# Revit family: TemID_Кронштейн настенный для биометрических терминалов_Rots-03 Stand
name_source: partatom
category: Охранная сигнализация
units: mm (PartAtom-declared; Revit-internal decimal feet)

## family parameters
Всегда вертикально = Нет
На основе рабочей плоскости = Нет
Общий = Да
При загрузке вырезать с полостями = Нет
Размер круглого соединителя = Использовать диаметр
Сохранять ориентацию аннотаций = Нет
Тип детали = Нормальный
Точка расчета площади = Да

## types (1)
- KJZ-03
    =Габариты= = =Габариты=
    ADSK_Единица измерения = шт.
    ADSK_Завод-изготовитель = TEMID
    ADSK_Количество = 1
    ADSK_Марка = KJZ-03
    ADSK_Наименование = Кронштейн крепления на турникет  для FaceDepot-7A/FaceDepot-7B/SpeedFace-V5
 FaceDepot-7BL/SpeedFaceV5L/ProFace X
FaceDepot-7BL[TD]/SpeedFace-V5L[TD].  80*38*370 мм
    ADSK_Раздел спецификации = 3. Периферийное оборудование
    ADSK_Размер_Высота = 110 мм
    ADSK_Размер_Глубина = 81 мм
    ADSK_Размер_Ширина = 88 мм
    ADSK_Тип = KJZ-03
    URL = https://temid-global.ru
    Зона обслуживания_Отступ от прибора = 50 мм
    Материал = Серый
    Отметка по умолчанию = 0 мм
    УГО_Тип = УГО_СКУД_Панель_вызова_видеодомофона : нет
